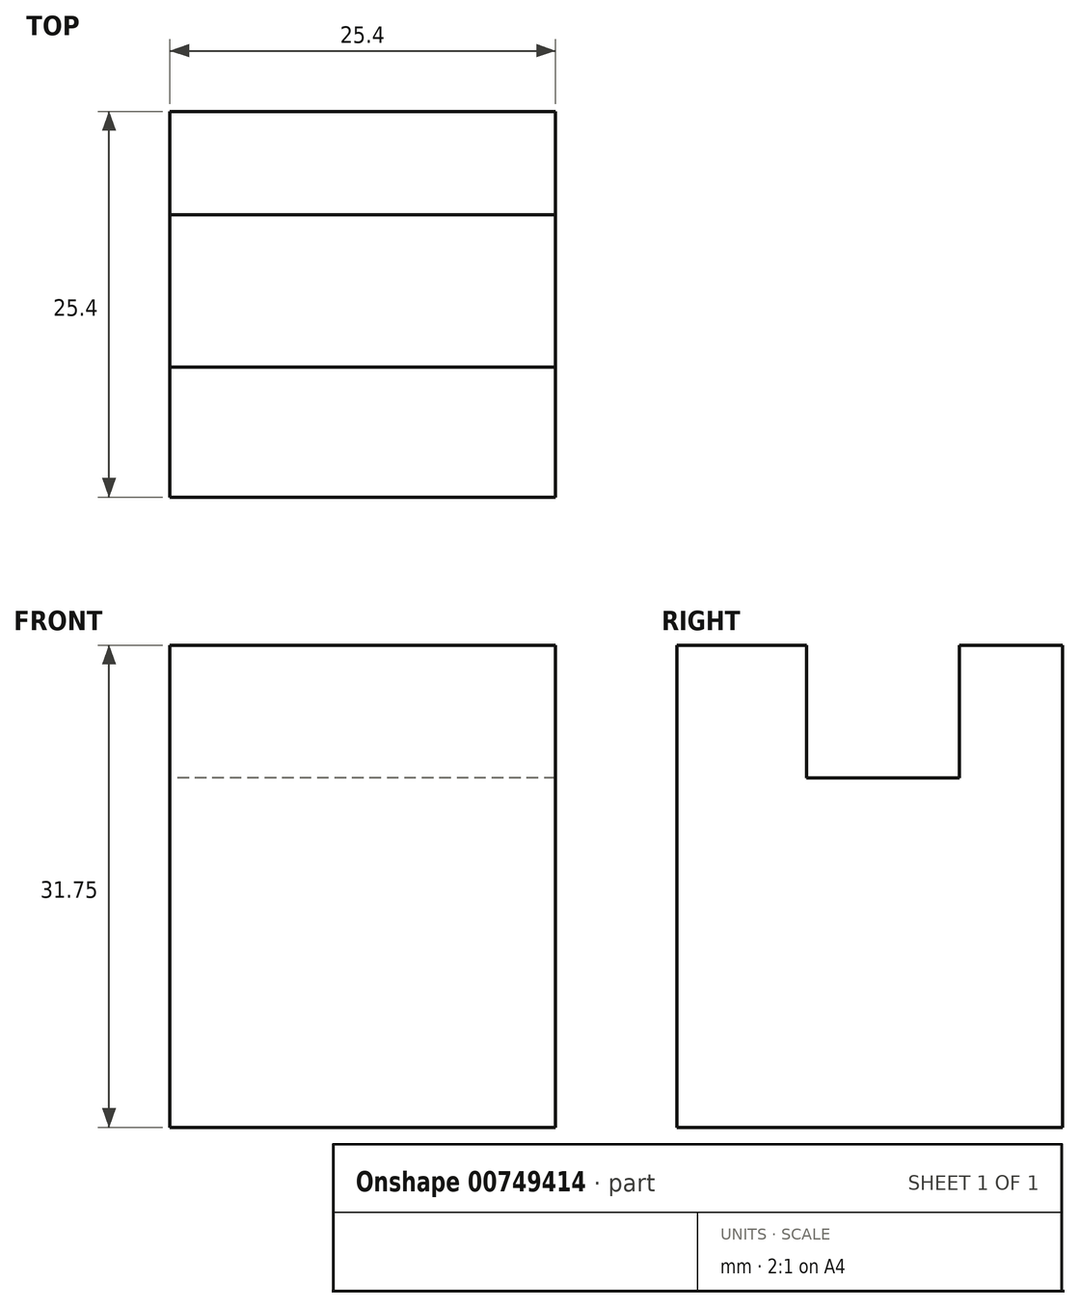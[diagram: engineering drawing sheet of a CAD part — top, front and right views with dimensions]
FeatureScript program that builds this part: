
annotation { "Feature Type Name" : "Feature", "Feature Type Description" : "" }
export const myFeature = defineFeature(function(context is Context, id is Id, definition is map)
    precondition{}
    {
        {
            var Q0;
            Q0=qCreatedBy(makeId("Right.planeOp"),FACE);
            var sketch = newSketch(context, id + "F0", { "sketchPlane" : qUnion([Q0])});
            skLineSegment(sketch, "E0", {"start": v(0, 31.75) * mm, "end": v(0, 0) * mm});
            skLineSegment(sketch, "E1", {"start": v(0, 0) * mm, "end": v(25.4, 0) * mm});
            skLineSegment(sketch, "E2", {"start": v(25.4, 0) * mm, "end": v(25.4, 31.75) * mm});
            skLineSegment(sketch, "E3", {"start": v(25.4, 31.75) * mm, "end": v(0, 31.75) * mm});
            skLineSegment(sketch, "E4", {"start": v(8.54, 31.75) * mm, "end": v(8.54, 23.02) * mm});
            skLineSegment(sketch, "E5", {"start": v(8.54, 23.02) * mm, "end": v(18.6, 23.02) * mm});
            skLineSegment(sketch, "E6", {"start": v(18.6, 23.02) * mm, "end": v(18.6, 31.75) * mm});
            skSolve(sketch);
        }
        {
            var Q0;
            {var subQ3=sQuery(id+"F0.wireOp",EDGE,"E0");Q0=makeQuery(id+"F0.imprint","IMPRINT",FACE,{"disambiguationData":[TD([[makeQuery(id+"F0.imprint","IMPRINT",EDGE,{"derivedFrom":subQ3}),1.0]])]});}
            extrude(context, id + "F1", {"entities" : qUnion([Q0]), "depth" : 25.4 * mm, "offsetDistance" : 25.4 * mm});
        }
    });
